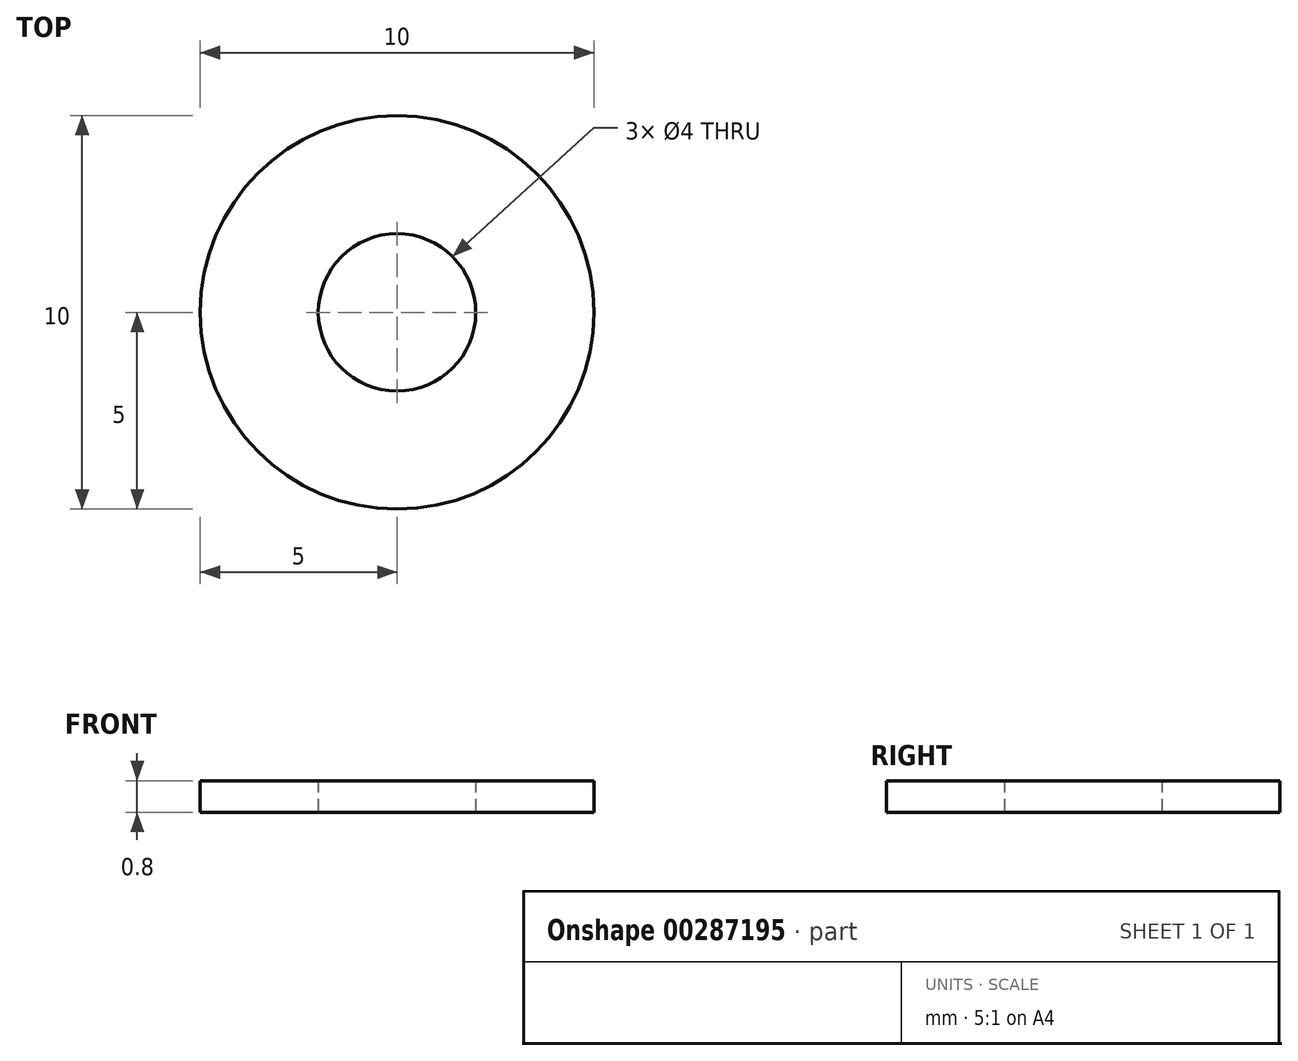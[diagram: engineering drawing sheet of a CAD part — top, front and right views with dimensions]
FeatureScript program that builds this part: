
annotation { "Feature Type Name" : "Feature", "Feature Type Description" : "" }
export const myFeature = defineFeature(function(context is Context, id is Id, definition is map)
    precondition{}
    {
        {
            var Q0;
            Q0=qCreatedBy(makeId("Top.planeOp"),FACE);
            var sketch = newSketch(context, id + "F0", { "sketchPlane" : qUnion([Q0])});
            skCircle(sketch, "E0", {"center": v(0, 0) * mm, "radius": 5 * mm});
            skCircle(sketch, "E1", {"center": v(0, 0) * mm, "radius": 2 * mm});
            skSolve(sketch);
        }
        {
            var Q0;
            Q0 = qSketchRegion(id + "F0", true);
            extrude(context, id + "F1", {"entities" : qUnion([Q0]), "depth" : 0.8 * mm});
        }
    });
